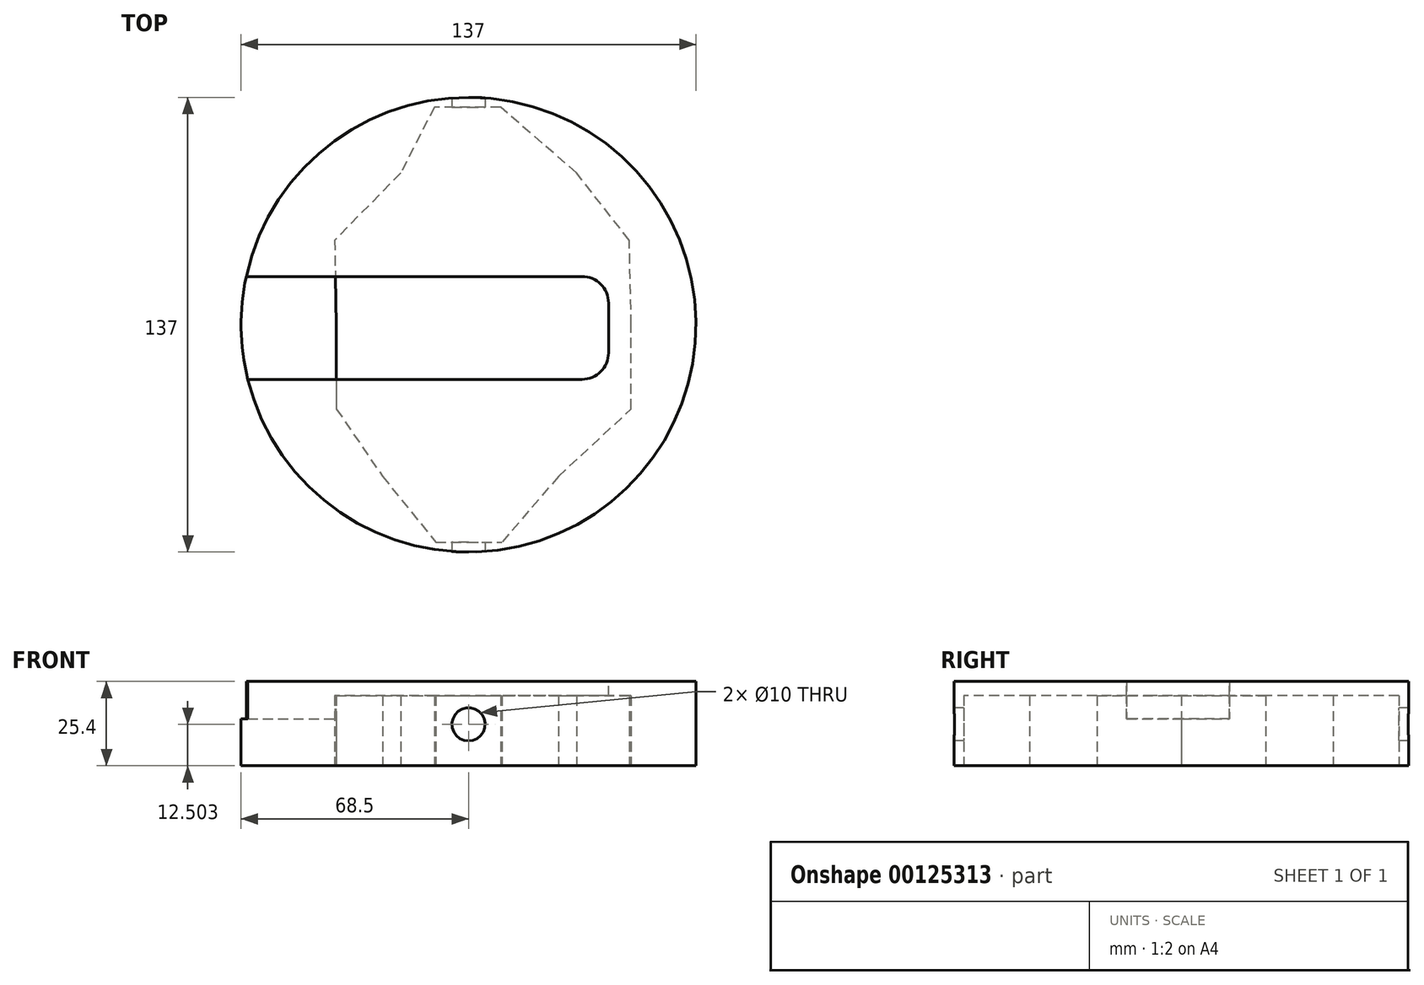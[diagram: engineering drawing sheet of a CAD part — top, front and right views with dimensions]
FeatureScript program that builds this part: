
annotation { "Feature Type Name" : "Feature", "Feature Type Description" : "" }
export const myFeature = defineFeature(function(context is Context, id is Id, definition is map)
    precondition{}
    {
        {
            var Q0;
            Q0=qCreatedBy(makeId("Top.planeOp"),FACE);
            var sketch = newSketch(context, id + "F0", { "sketchPlane" : qUnion([Q0])});
            skCircle(sketch, "E0", {"center": v(0, 0) * mm, "radius": 68.5 * mm});
            skSolve(sketch);
        }
        {
            var Q0;
            Q0 = qSketchRegion(id + "F0", true);
            extrude(context, id + "F1", {"entities" : qUnion([Q0]), "depth" : 25.4 * mm});
        }
        {
            var Q0;
            Q0=makeQuery(id+"F1.opExtrude","CAP_FACE",FACE,{"disambiguationData":[OSD([sQuery(id+"F0.wireOp",EDGE,"E0")])],"isStart":false});
            var sketch = newSketch(context, id + "F2", { "sketchPlane" : qUnion([Q0])});
            skLineSegment(sketch, "E1.bottom", {"start": v(-88.3, 14.53) * mm, "end": v(34.15, 14.53) * mm});
            skLineSegment(sketch, "E1.top", {"start": v(-88.3, -16.46) * mm, "end": v(34.15, -16.46) * mm});
            skLineSegment(sketch, "E1.left", {"start": v(-88.3, 14.53) * mm, "end": v(-88.3, -16.46) * mm});
            skLineSegment(sketch, "E1.right", {"start": v(42.15, 6.53) * mm, "end": v(42.15, -8.46) * mm});
            skPoint(sketch, "E1.middle", {"position": v(0, 0) * mm});
            skPoint(sketch, "E2.visualSharp", {"position": v(42.15, 14.53) * mm});
            skArc(sketch, "E2.filletArc", {"start": v(42.15, 6.53) * mm, "mid": v(39.8, 12.18) * mm, "end": v(34.15, 14.53) * mm});
            skPoint(sketch, "E3.visualSharp", {"position": v(42.15, -16.46) * mm});
            skArc(sketch, "E3.filletArc", {"start": v(34.15, -16.46) * mm, "mid": v(39.8, -14.12) * mm, "end": v(42.15, -8.46) * mm});
            skSolve(sketch);
        }
        {
            var Q0;
            Q0 = qSketchRegion(id + "F2", true);
            extrude(context, id + "F3", {"entities" : qUnion([Q0]), "operationType" : NewBodyOperationType.REMOVE, "oppositeDirection" : true, "depth" : 11.25 * mm});
        }
        {
            var Q0;
            Q0=qCreatedBy(makeId("Front.planeOp"),FACE);
            var sketch = newSketch(context, id + "F4", { "sketchPlane" : qUnion([Q0])});
            skPoint(sketch, "E4", {"position": v(0, 12.5) * mm});
            skCircle(sketch, "E5", {"center": v(0, 12.5) * mm, "radius": 5 * mm});
            skSolve(sketch);
        }
        {
            var Q0;
            Q0=makeQuery(id+"F1.opExtrude","CAP_FACE",FACE,{"disambiguationData":[OSD([sQuery(id+"F0.wireOp",EDGE,"E0")])],"isStart":true});
            var sketch = newSketch(context, id + "F5", { "sketchPlane" : qUnion([Q0])});
            skPoint(sketch, "E6", {"position": v(0, 65.53) * mm});
            skPoint(sketch, "E7", {"position": v(10.13, 65.53) * mm});
            skPoint(sketch, "E8", {"position": v(-9.83, 65.53) * mm});
            skPoint(sketch, "E9", {"position": v(0, 45.72) * mm});
            skPoint(sketch, "E10", {"position": v(27.09, 45.72) * mm});
            skPoint(sketch, "E11", {"position": v(-25.9, 45.72) * mm});
            skPoint(sketch, "E12", {"position": v(0, 25.4) * mm});
            skPoint(sketch, "E13", {"position": v(48.98, 25.4) * mm});
            skPoint(sketch, "E14", {"position": v(-39.78, 25.4) * mm});
            skPoint(sketch, "E15", {"position": v(-39.78, 0) * mm});
            skPoint(sketch, "E16", {"position": v(48.98, 0) * mm});
            skPoint(sketch, "E17", {"position": v(0, -25.4) * mm});
            skPoint(sketch, "E18", {"position": v(0, -45.72) * mm});
            skPoint(sketch, "E19", {"position": v(0, -65.53) * mm});
            skPoint(sketch, "E20", {"position": v(-40.31, -25.4) * mm});
            skPoint(sketch, "E21", {"position": v(48.44, -25.4) * mm});
            skPoint(sketch, "E22", {"position": v(-20.45, -45.72) * mm});
            skPoint(sketch, "E23", {"position": v(32.54, -45.72) * mm});
            skPoint(sketch, "E24", {"position": v(-10.3, -65.53) * mm});
            skPoint(sketch, "E25", {"position": v(9.66, -65.53) * mm});
            skLineSegment(sketch, "E26", {"start": v(-9.83, 65.53) * mm, "end": v(10.13, 65.53) * mm});
            skLineSegment(sketch, "E27", {"start": v(27.09, 45.72) * mm, "end": v(10.13, 65.53) * mm});
            skLineSegment(sketch, "E28", {"start": v(27.09, 45.72) * mm, "end": v(48.98, 25.4) * mm});
            skLineSegment(sketch, "E29", {"start": v(48.98, 25.4) * mm, "end": v(48.98, 0) * mm});
            skLineSegment(sketch, "E30", {"start": v(48.98, 0) * mm, "end": v(48.44, -25.4) * mm});
            skLineSegment(sketch, "E31", {"start": v(48.44, -25.4) * mm, "end": v(32.54, -45.72) * mm});
            skLineSegment(sketch, "E32", {"start": v(32.54, -45.72) * mm, "end": v(9.66, -65.53) * mm});
            skLineSegment(sketch, "E33", {"start": v(9.66, -65.53) * mm, "end": v(-10.3, -65.53) * mm});
            skLineSegment(sketch, "E34", {"start": v(-10.3, -65.53) * mm, "end": v(-20.45, -45.72) * mm});
            skLineSegment(sketch, "E35", {"start": v(-20.45, -45.72) * mm, "end": v(-40.31, -25.4) * mm});
            skLineSegment(sketch, "E36", {"start": v(-40.31, -25.4) * mm, "end": v(-39.78, 0) * mm});
            skLineSegment(sketch, "E37", {"start": v(-39.78, 0) * mm, "end": v(-39.78, 25.4) * mm});
            skLineSegment(sketch, "E38", {"start": v(-39.78, 25.4) * mm, "end": v(-25.9, 45.72) * mm});
            skLineSegment(sketch, "E39", {"start": v(-25.9, 45.72) * mm, "end": v(-9.83, 65.53) * mm});
            skSolve(sketch);
        }
        {
            var Q0;
            Q0=makeQuery(id+"F5.imprint","IMPRINT",FACE,{"disambiguationData":[TD([[makeQuery(id+"F5.imprint","IMPRINT",EDGE,{"derivedFrom":sQuery(id+"F5.wireOp",EDGE,"E26")}),-1.0]])]});
            extrude(context, id + "F6", {"entities" : qUnion([Q0]), "operationType" : NewBodyOperationType.REMOVE, "oppositeDirection" : true, "depth" : 21.08 * mm});
        }
        {
            var Q0;
            Q0=makeQuery(id+"F4.imprint","IMPRINT",FACE,{"disambiguationData":[TD([[makeQuery(id+"F4.imprint","IMPRINT",EDGE,{"derivedFrom":sQuery(id+"F4.wireOp",EDGE,"E5")}),1.0]])]});
            extrude(context, id + "F7", {"entities" : qUnion([Q0]), "operationType" : NewBodyOperationType.REMOVE, "endBound" : BoundingType.THROUGH_ALL, "oppositeDirection" : true, "depth" : 25.4 * mm, "hasSecondDirection" : true, "secondDirectionBound" : SecondDirectionBoundingType.THROUGH_ALL, "secondDirectionOppositeDirection" : false, "secondDirectionDepth" : 25.4 * mm});
        }
    });
